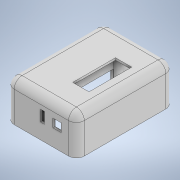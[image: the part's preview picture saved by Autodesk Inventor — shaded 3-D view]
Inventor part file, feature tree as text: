
AUTODESK INVENTOR PART (.ipt)
format: ipt  version: 2021.2 (Build 252289000, 289)  size: 514,560 bytes
history: native  units: mm
features: extrude x19, sketch x19, fillet x4, chamfer x4, other x3, shell x1, projected_geometry x1
ambient origin geometry x8: Origin, YZ Plane, XZ Plane, XY Plane, X Axis, Y Axis, Z Axis, Center Point
bodies: Body1 (feature_tree)
feature tree (51):
  other  "Твердое тело1"
  extrude  "Выдавливание1"  Depth=50.0mm
  fillet  "Сопряжение1"  Radius=70.0mm
  shell  "Оболочка1"  Thickness=30.0mm
  extrude  "Выдавливание3"  Depth=5.0mm
  extrude  "Выдавливание4"  Depth=1.6mm
  fillet  "Сопряжение2"  Radius=1.2mm
  extrude  "Выдавливание6"  Depth=1.2mm
  extrude  "Выдавливание7"  Depth=1.2mm
  extrude  "Датчик"  Depth=1.2mm
  extrude  "usb зарядка"  Depth=5.0mm
  extrude  "Кнопка"  Depth=12.0mm
  extrude  "Выдавливание10"  Depth=31.5mm
  extrude  "Выдавливание11"  Depth=5.0mm
  chamfer  "Фаска1"  Distance=14.25mm
  extrude  "Выдавливание12"  Depth=14.25mm
  chamfer  "Фаска2"  Distance=10.0mm
  extrude  "Выдавливание13"  Depth=20.0mm TaperAngle=0.0deg
  chamfer  "Фаска3"  Distance=5.8mm
  extrude  "Выдавливание14"  Depth=6.2mm
  chamfer  "Фаска4"  Distance=6.2mm
  extrude  "Выдавливание15"  Depth=5.5mm
  extrude  "Выдавливание16"  Depth=20.0mm TaperAngle=0.0deg
  fillet  "Сопряжение3"  Radius=5.0mm
  extrude  "Выдавливание17"  Depth=5.0mm
  sketch  "Эскиз18"
  extrude  "Выдавливание18"  Depth=5.0mm
  fillet  "Сопряжение4"  Radius=4.3mm
  extrude  "Выдавливание19"  Depth=7.1mm
  extrude  "Выдавливание20"  Depth=4.3mm
  other  "Удаление грани1"
  other  "Удаление грани2"
  sketch  "Эскиз1"
  sketch  "Эскиз3"
  sketch  "Эскиз4"
  sketch  "Эскиз5"
  sketch  "Эскиз6"
  sketch  "Эскиз7"
  sketch  "Эскиз8"
  sketch  "Эскиз9"
  sketch  "Эскиз10"
  projected_geometry  "Спроецированная петля1"
  sketch  "Эскиз11"
  sketch  "Эскиз12"
  sketch  "Эскиз13"
  sketch  "Эскиз14"
  sketch  "Эскиз15"
  sketch  "Эскиз16"
  sketch  "Эскиз17"
  sketch  "Эскиз20"
  sketch  "Эскиз21"
